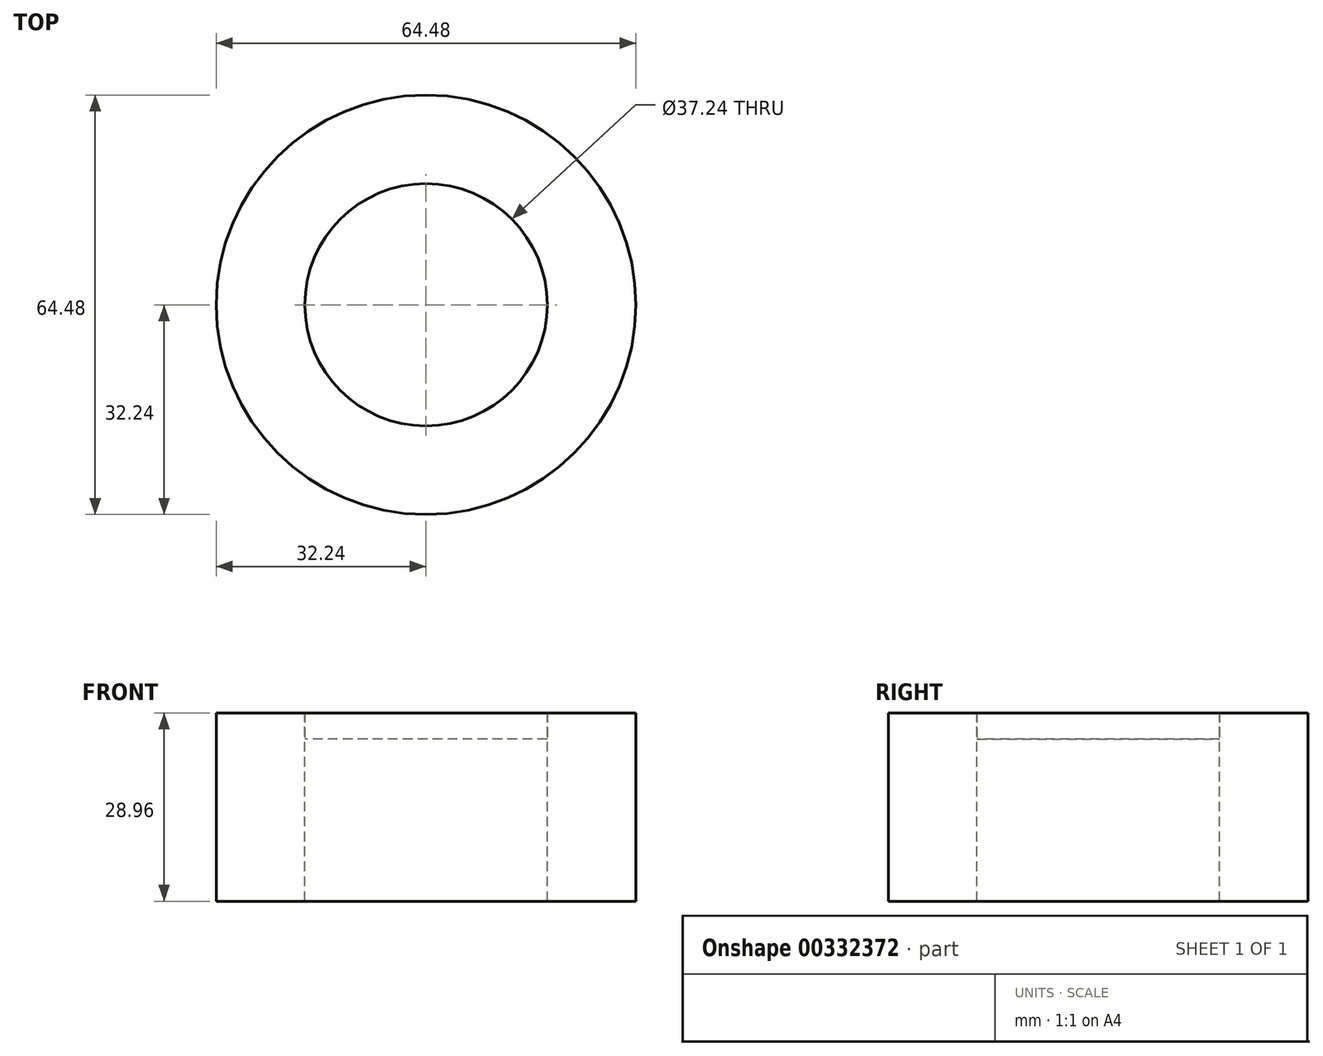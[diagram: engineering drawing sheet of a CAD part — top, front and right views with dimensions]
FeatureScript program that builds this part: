
annotation { "Feature Type Name" : "Feature", "Feature Type Description" : "" }
export const myFeature = defineFeature(function(context is Context, id is Id, definition is map)
    precondition{}
    {
        {
            var Q0;
            Q0=qCreatedBy(makeId("Top.planeOp"),FACE);
            var sketch = newSketch(context, id + "F0", { "sketchPlane" : qUnion([Q0])});
            skCircle(sketch, "E0", {"center": v(0, 0) * mm, "radius": 18.62 * mm});
            skSolve(sketch);
        }
        {
            var Q0;
            Q0=makeQuery(id+"F0.imprint","IMPRINT",FACE,{"disambiguationData":[TD([[makeQuery(id+"F0.imprint","IMPRINT",EDGE,{"derivedFrom":sQuery(id+"F0.wireOp",EDGE,"E0")}),1.0]])]});
            extrude(context, id + "F1", {"entities" : qUnion([Q0]), "depth" : 4 * mm});
        }
        {
            var Q0;
            Q0=makeQuery(id+"F1.opExtrude","CAP_FACE",FACE,{"disambiguationData":[OSD([sQuery(id+"F0.wireOp",EDGE,"E0")])],"isStart":false});
            var sketch = newSketch(context, id + "F2", { "sketchPlane" : qUnion([Q0])});
            skCircle(sketch, "E1", {"center": v(0, 0) * mm, "radius": 32.24 * mm});
            skSolve(sketch);
        }
        {
            var Q0;
            Q0=makeQuery(id+"F2.imprint","IMPRINT",FACE,{"disambiguationData":[TD([[makeQuery(id+"F2.imprint","IMPRINT",EDGE,{"derivedFrom":sQuery(id+"F2.wireOp",EDGE,"E1")}),1.0]])]});
            extrude(context, id + "F3", {"entities" : qUnion([Q0]), "oppositeDirection" : true, "depth" : 28.96 * mm});
        }
    });
